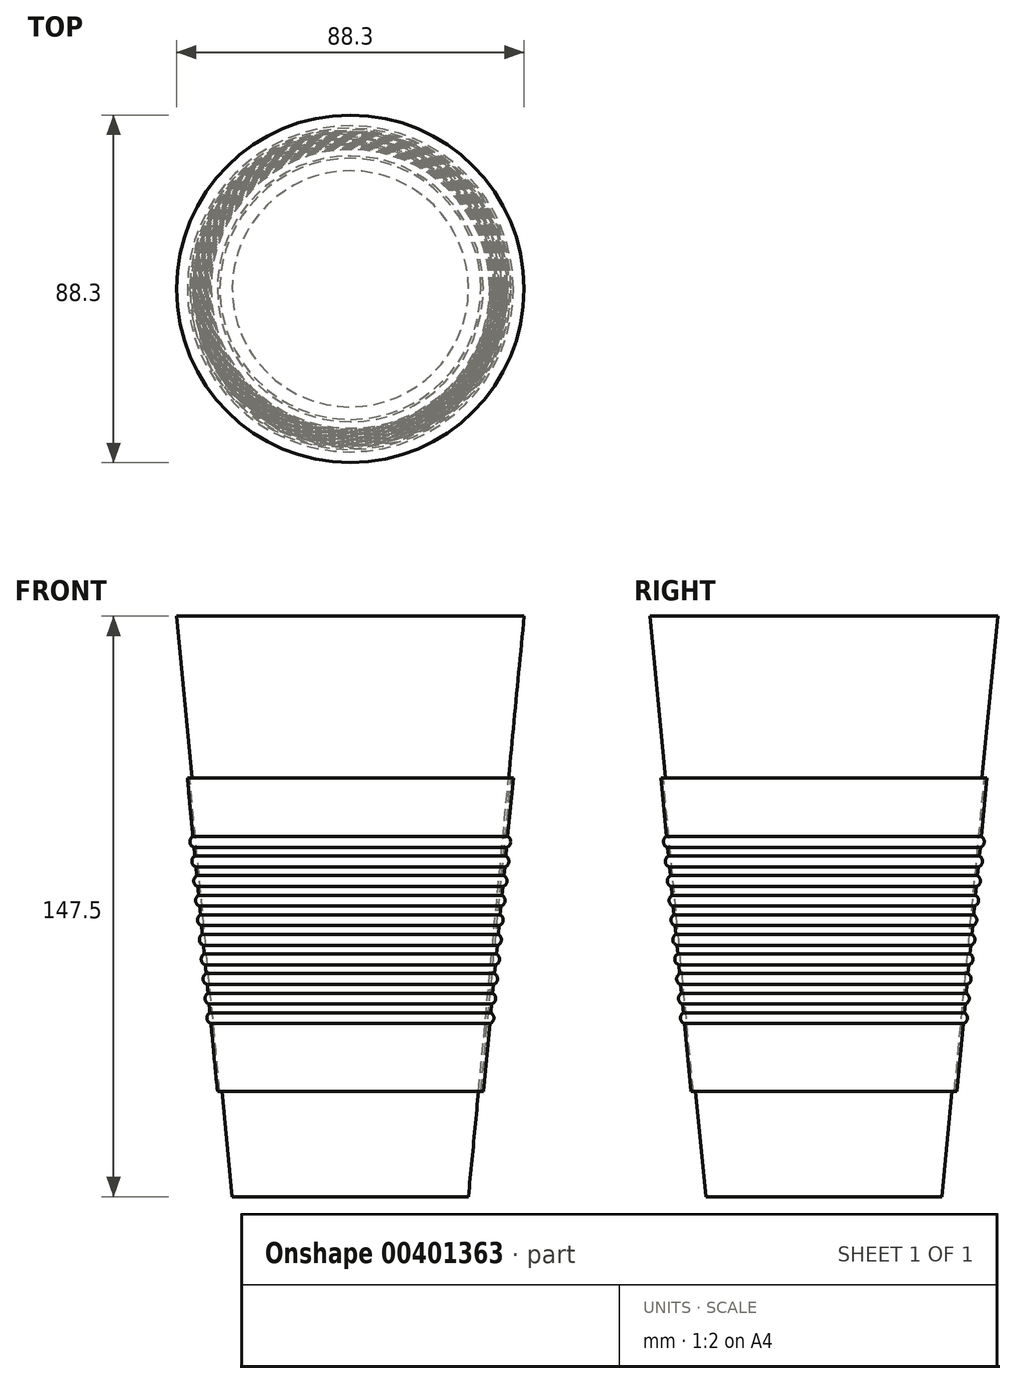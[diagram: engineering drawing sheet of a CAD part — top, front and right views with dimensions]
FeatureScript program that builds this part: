
annotation { "Feature Type Name" : "Feature", "Feature Type Description" : "" }
export const myFeature = defineFeature(function(context is Context, id is Id, definition is map)
    precondition{}
    {
        {
            var Q0;
            Q0=qCreatedBy(makeId("Top.planeOp"),FACE);
            var sketch = newSketch(context, id + "F0", { "sketchPlane" : qUnion([Q0])});
            skCircle(sketch, "E0", {"center": v(0, 0) * mm, "radius": 30 * mm});
            skSolve(sketch);
        }
        {
            var Q0;
            Q0=qCreatedBy(makeId("Top.planeOp"),FACE);
            cPlane(context, id + "F1", {"entities" : qUnion([Q0]), "cplaneType" : CPlaneType.OFFSET, "offset" : 147.5 * mm, "width" : 150 * mm, "height" : 150 * mm});
        }
        {
            var Q0;
            Q0=qCreatedBy(id+"F1.planeOp",FACE);
            var sketch = newSketch(context, id + "F2", { "sketchPlane" : qUnion([Q0])});
            skCircle(sketch, "E1", {"center": v(0, 0) * mm, "radius": 44.15 * mm});
            skSolve(sketch);
        }
        {
            var Q0;
            Q0=makeQuery(id+"F0.imprint","IMPRINT",FACE,{"disambiguationData":[TD([[makeQuery(id+"F0.imprint","IMPRINT",EDGE,{"derivedFrom":sQuery(id+"F0.wireOp",EDGE,"E0")}),1.0]])]});
            var Q1;
            Q1=makeQuery(id+"F2.imprint","IMPRINT",FACE,{"disambiguationData":[TD([[makeQuery(id+"F2.imprint","IMPRINT",EDGE,{"derivedFrom":sQuery(id+"F2.wireOp",EDGE,"E1")}),1.0]])]});
            loft(context, id + "F3", {"sheetProfilesArray" : [{ "sheetProfileEntities" : qUnion([Q0]) }, { "sheetProfileEntities" : qUnion([Q1]) }]});
        }
        {
            var Q0;
            Q0=qCreatedBy(makeId("Front.planeOp"),FACE);
            var sketch = newSketch(context, id + "F4", { "sketchPlane" : qUnion([Q0])});
            skLineSegment(sketch, "E2", {"start": v(44.15, 147.5) * mm, "end": v(30, 0) * mm, "construction": true});
            skLineSegment(sketch, "E3", {"start": v(-30, 0) * mm, "end": v(-44.15, 147.5) * mm, "construction": true});
            skLineSegment(sketch, "E4", {"start": v(0, 0) * mm, "end": v(0, 147.5) * mm, "construction": true});
            skLineSegment(sketch, "E5", {"start": v(-40.21, 106.44) * mm, "end": v(-40.81, 106.44) * mm, "construction": true});
            skLineSegment(sketch, "E6", {"start": v(-40.81, 106.44) * mm, "end": v(-33.18, 26.86) * mm});
            skLineSegment(sketch, "E7", {"start": v(-33.18, 26.86) * mm, "end": v(-33.77, 26.8) * mm});
            skLineSegment(sketch, "E8", {"start": v(-33.77, 26.8) * mm, "end": v(-41.41, 106.44) * mm});
            skLineSegment(sketch, "E9", {"start": v(-41.41, 106.44) * mm, "end": v(-40.81, 106.44) * mm});
            skArc(sketch, "E10", {"start": v(-39.98, 91.5) * mm, "mid": v(-40.75, 90.05) * mm, "end": v(-39.72, 88.77) * mm});
            skArc(sketch, "E11.1.0.0", {"start": v(-39.5, 86.53) * mm, "mid": v(-40.27, 85.07) * mm, "end": v(-39.24, 83.79) * mm});
            skArc(sketch, "E11.2.0.0", {"start": v(-39.02, 81.55) * mm, "mid": v(-39.8, 80.1) * mm, "end": v(-38.76, 78.81) * mm});
            skArc(sketch, "E11.3.0.0", {"start": v(-38.55, 76.57) * mm, "mid": v(-39.31, 75.12) * mm, "end": v(-38.28, 73.83) * mm});
            skArc(sketch, "E11.4.0.0", {"start": v(-38.07, 71.6) * mm, "mid": v(-38.84, 70.14) * mm, "end": v(-37.8, 68.86) * mm});
            skArc(sketch, "E11.5.0.0", {"start": v(-37.6, 66.62) * mm, "mid": v(-38.36, 65.16) * mm, "end": v(-37.33, 63.88) * mm});
            skArc(sketch, "E11.6.0.0", {"start": v(-37.11, 61.64) * mm, "mid": v(-37.88, 60.19) * mm, "end": v(-36.85, 58.9) * mm});
            skArc(sketch, "E11.7.0.0", {"start": v(-36.64, 56.66) * mm, "mid": v(-37.4, 55.2) * mm, "end": v(-36.37, 53.92) * mm});
            skArc(sketch, "E11.8.0.0", {"start": v(-36.16, 51.69) * mm, "mid": v(-36.93, 50.23) * mm, "end": v(-35.9, 48.95) * mm});
            skArc(sketch, "E11.9.0.0", {"start": v(-35.68, 46.71) * mm, "mid": v(-36.45, 45.25) * mm, "end": v(-35.42, 43.97) * mm});
            skLineSegment(sketch, "E11.direction1", {"start": v(-39.72, 88.77) * mm, "end": v(-39.24, 83.79) * mm, "construction": true});
            skLineSegment(sketch, "E12", {"start": v(-41.41, 106.44) * mm, "end": v(-39.98, 91.5) * mm, "construction": true});
            skSolve(sketch);
        }
        {
            var Q0;
            Q0=makeQuery(id+"F4.imprint","IMPRINT",FACE,{"disambiguationData":[TD([[makeQuery(id+"F4.imprint","IMPRINT",EDGE,{"derivedFrom":sQuery(id+"F4.wireOp",EDGE,"E6")}),-1.0]])]});
            var Q1;
            {var subQ0=sQuery(id+"F4.wireOp",EDGE,"E10");Q1=makeQuery(id+"F4.imprint","IMPRINT",FACE,{"disambiguationData":[TD([[makeQuery(id+"F4.imprint","IMPRINT",EDGE,{"derivedFrom":subQ0}),1.0]])]});}
            var Q2;
            {var subQ0=sQuery(id+"F4.wireOp",EDGE,"E11.1.0.0");Q2=makeQuery(id+"F4.imprint","IMPRINT",FACE,{"disambiguationData":[TD([[makeQuery(id+"F4.imprint","IMPRINT",EDGE,{"derivedFrom":subQ0}),1.0]])]});}
            var Q3;
            {var subQ0=sQuery(id+"F4.wireOp",EDGE,"E11.2.0.0");Q3=makeQuery(id+"F4.imprint","IMPRINT",FACE,{"disambiguationData":[TD([[makeQuery(id+"F4.imprint","IMPRINT",EDGE,{"derivedFrom":subQ0}),1.0]])]});}
            var Q4;
            {var subQ0=sQuery(id+"F4.wireOp",EDGE,"E11.3.0.0");Q4=makeQuery(id+"F4.imprint","IMPRINT",FACE,{"disambiguationData":[TD([[makeQuery(id+"F4.imprint","IMPRINT",EDGE,{"derivedFrom":subQ0}),1.0]])]});}
            var Q5;
            {var subQ0=sQuery(id+"F4.wireOp",EDGE,"E11.4.0.0");Q5=makeQuery(id+"F4.imprint","IMPRINT",FACE,{"disambiguationData":[TD([[makeQuery(id+"F4.imprint","IMPRINT",EDGE,{"derivedFrom":subQ0}),1.0]])]});}
            var Q6;
            {var subQ0=sQuery(id+"F4.wireOp",EDGE,"E11.5.0.0");Q6=makeQuery(id+"F4.imprint","IMPRINT",FACE,{"disambiguationData":[TD([[makeQuery(id+"F4.imprint","IMPRINT",EDGE,{"derivedFrom":subQ0}),1.0]])]});}
            var Q7;
            {var subQ0=sQuery(id+"F4.wireOp",EDGE,"E11.6.0.0");Q7=makeQuery(id+"F4.imprint","IMPRINT",FACE,{"disambiguationData":[TD([[makeQuery(id+"F4.imprint","IMPRINT",EDGE,{"derivedFrom":subQ0}),1.0]])]});}
            var Q8;
            {var subQ0=sQuery(id+"F4.wireOp",EDGE,"E11.7.0.0");Q8=makeQuery(id+"F4.imprint","IMPRINT",FACE,{"disambiguationData":[TD([[makeQuery(id+"F4.imprint","IMPRINT",EDGE,{"derivedFrom":subQ0}),1.0]])]});}
            var Q9;
            {var subQ0=sQuery(id+"F4.wireOp",EDGE,"E11.8.0.0");Q9=makeQuery(id+"F4.imprint","IMPRINT",FACE,{"disambiguationData":[TD([[makeQuery(id+"F4.imprint","IMPRINT",EDGE,{"derivedFrom":subQ0}),1.0]])]});}
            var Q10;
            {var subQ0=sQuery(id+"F4.wireOp",EDGE,"E11.9.0.0");Q10=makeQuery(id+"F4.imprint","IMPRINT",FACE,{"disambiguationData":[TD([[makeQuery(id+"F4.imprint","IMPRINT",EDGE,{"derivedFrom":subQ0}),1.0]])]});}
            var Q11;
            Q11=sQuery(id+"F4.wireOp",EDGE,"E4");
            revolve(context, id + "F5", {"entities" : qUnion([Q0, Q1, Q2, Q3, Q4, Q5, Q6, Q7, Q8, Q9, Q10]), "axis" : qUnion([Q11]), "revolveType" : RevolveType.FULL});
        }
    });
